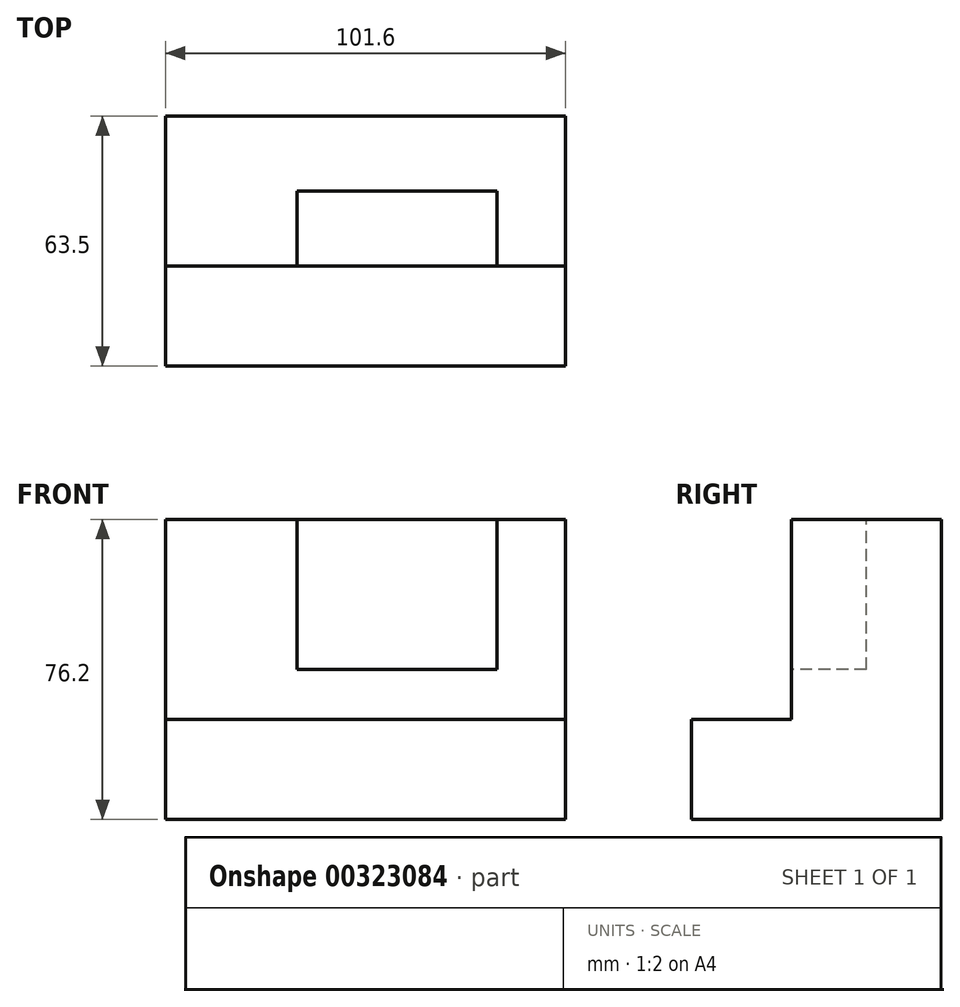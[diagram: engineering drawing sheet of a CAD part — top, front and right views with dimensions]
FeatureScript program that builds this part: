
annotation { "Feature Type Name" : "Feature", "Feature Type Description" : "" }
export const myFeature = defineFeature(function(context is Context, id is Id, definition is map)
    precondition{}
    {
        {
            var Q0;
            Q0=qCreatedBy(makeId("Right.planeOp"),FACE);
            var sketch = newSketch(context, id + "F0", { "sketchPlane" : qUnion([Q0])});
            skLineSegment(sketch, "E0", {"start": v(17.6, 18.45) * mm, "end": v(17.6, -57.75) * mm});
            skLineSegment(sketch, "E1", {"start": v(17.6, -57.75) * mm, "end": v(-45.9, -57.75) * mm});
            skLineSegment(sketch, "E2", {"start": v(-45.9, -57.75) * mm, "end": v(-45.9, -32.35) * mm});
            skLineSegment(sketch, "E3", {"start": v(-45.9, -32.35) * mm, "end": v(-20.5, -32.35) * mm});
            skLineSegment(sketch, "E4", {"start": v(-20.5, -32.35) * mm, "end": v(-20.5, 18.45) * mm});
            skLineSegment(sketch, "E5", {"start": v(-20.5, 18.45) * mm, "end": v(17.6, 18.45) * mm});
            skSolve(sketch);
        }
        {
            var Q0;
            Q0=makeQuery(id+"F0.imprint","IMPRINT",FACE,{"disambiguationData":[TD([[makeQuery(id+"F0.imprint","IMPRINT",EDGE,{"derivedFrom":sQuery(id+"F0.wireOp",EDGE,"E0")}),-1.0]])]});
            extrude(context, id + "F1", {"entities" : qUnion([Q0]), "depth" : 101.6 * mm});
        }
        {
            var Q0;
            Q0=makeQuery(id+"F1.opExtrude","SWEPT_FACE",FACE,{"disambiguationData":[OSD([sQuery(id+"F0.wireOp",EDGE,"E4")])]});
            var sketch = newSketch(context, id + "F2", { "sketchPlane" : qUnion([Q0])});
            skLineSegment(sketch, "E6", {"start": v(33.43, -19.65) * mm, "end": v(84.23, -19.65) * mm});
            skLineSegment(sketch, "E7", {"start": v(84.23, -19.65) * mm, "end": v(84.23, 18.45) * mm});
            skLineSegment(sketch, "E8", {"start": v(33.43, -19.65) * mm, "end": v(33.43, 18.45) * mm});
            skSolve(sketch);
        }
        {
            var Q0;
            Q0 = qSketchRegion(id + "F2", true);
            var Q1;
            Q1=makeQuery(id+"F2.imprint","IMPRINT",FACE,{"disambiguationData":[TD([[makeQuery(id+"F2.imprint","IMPRINT",EDGE,{"derivedFrom":sQuery(id+"F2.wireOp",EDGE,"E6")}),1.0]])]});
            extrude(context, id + "F3", {"entities" : qUnion([Q0, Q1]), "operationType" : NewBodyOperationType.REMOVE, "oppositeDirection" : true, "depth" : 19.05 * mm});
        }
    });
